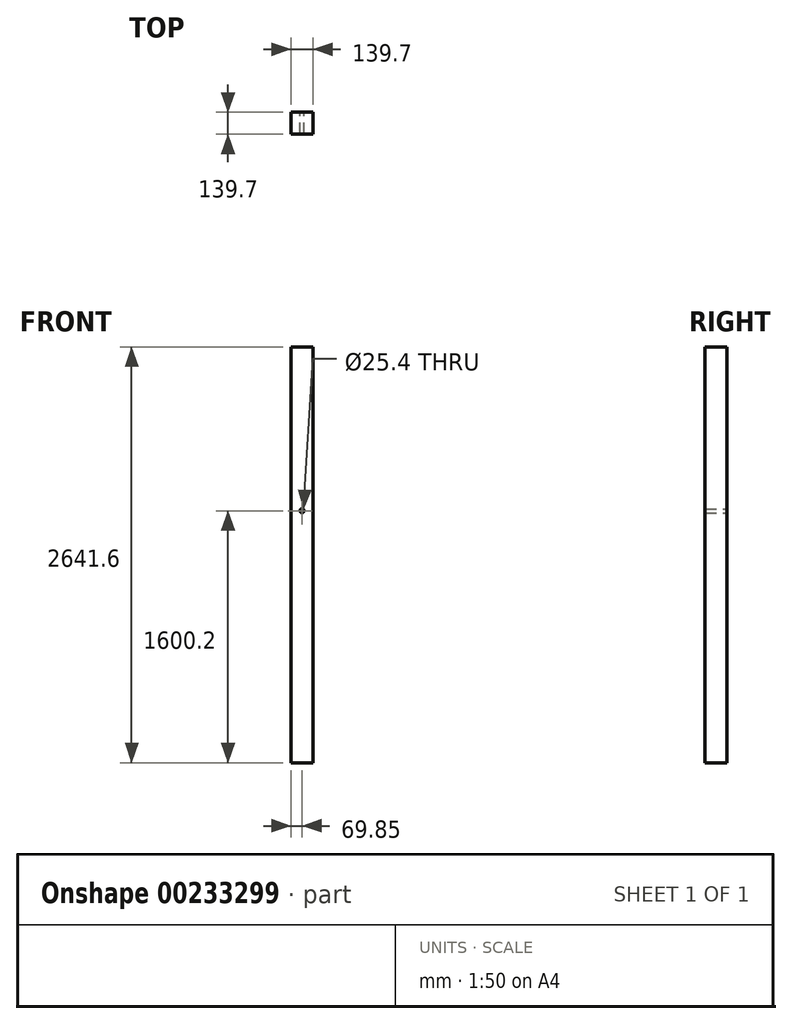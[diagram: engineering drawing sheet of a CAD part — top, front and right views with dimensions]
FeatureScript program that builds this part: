
annotation { "Feature Type Name" : "Feature", "Feature Type Description" : "" }
export const myFeature = defineFeature(function(context is Context, id is Id, definition is map)
    precondition{}
    {
        {
            var Q0;
            Q0=qCreatedBy(makeId("Front.planeOp"),FACE);
            var sketch = newSketch(context, id + "F0", { "sketchPlane" : qUnion([Q0])});
            skLineSegment(sketch, "E0", {"start": v(-69.85, -91.96) * mm, "end": v(69.85, -91.96) * mm});
            skLineSegment(sketch, "E1", {"start": v(-69.85, -91.96) * mm, "end": v(-69.85, 2549.64) * mm});
            skLineSegment(sketch, "E2", {"start": v(-69.85, 2549.64) * mm, "end": v(69.85, 2549.64) * mm});
            skLineSegment(sketch, "E3", {"start": v(69.85, 2549.64) * mm, "end": v(69.85, -91.96) * mm});
            skCircle(sketch, "E4", {"center": v(0, 1508.24) * mm, "radius": 12.7 * mm});
            skSolve(sketch);
        }
        {
            var Q0;
            Q0=makeQuery(id+"F0.imprint","IMPRINT",FACE,{"disambiguationData":[TD([[makeQuery(id+"F0.imprint","IMPRINT",EDGE,{"derivedFrom":sQuery(id+"F0.wireOp",EDGE,"E0")}),1.0]])]});
            extrude(context, id + "F1", {"entities" : qUnion([Q0]), "depth" : 139.7 * mm});
        }
    });
